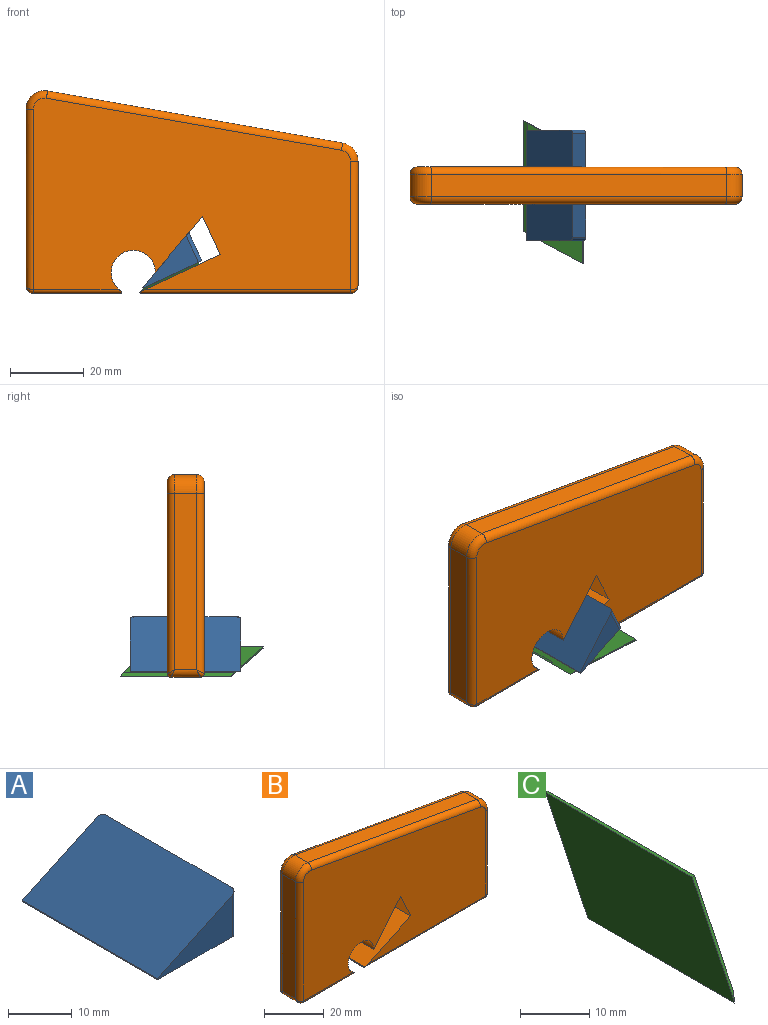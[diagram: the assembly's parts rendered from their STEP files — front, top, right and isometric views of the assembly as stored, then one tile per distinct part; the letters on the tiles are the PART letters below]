
ASSEMBLY  parts=3 mates=2
PART A: 8 faces, bbox 17.5x30x8.4 mm
  f0: plane 30x17.55mm, normal (-0.42,0,0.91), area 580.4mm2, adj f2,f3,f4,f5,f6,f7
  f1: plane 30x17.5mm, normal (0,0,-1), area 524.6mm2, adj f2,f3,f4,f5,f6,f7
  f2: plane 28x8.39mm, normal (1,0,0), area 235mm2, adj f0,f1,f6,f7
  f3: plane 16.55x7.93mm, normal (0,-1,0), area 67.3mm2, adj f0,f1,f5,f7
  f4: plane 16.55x7.93mm, normal (0,1,0), area 67.3mm2, adj f0,f1,f5,f6
  f5: plane 30x0.21mm, normal (-0.98,0,-0.22), area 6.5mm2, adj f0,f1,f3,f4
  f6: cylinder r=1mm len=8.39mm, axis (0,0,1), area 12.9mm2, adj f0,f1,f2,f4
  f7: cylinder r=1mm len=8.39mm, axis (0,0,-1), area 12.9mm2, adj f0,f1,f2,f3
PART B: 35 faces, bbox 90.9x10x55.4 mm
  f0: plane 57x8mm, normal (0,0,-1), area 456mm2, adj f7,f24,f31,f33
  f1: plane 86x51.91mm, normal (0,-1,0), area 3618.9mm2, adj f8,f9,f10,f11,f19,f21,f23,f25
  f2: plane 86x51.91mm, normal (0,1,0), area 3618.9mm2, adj f8,f9,f10,f11,f15,f16,f18,f20
  f3: plane 47.91x6mm, normal (-1,0,0), area 287.5mm2, adj f14,f15,f17,f19
  f4: plane 24x8mm, normal (0,0,-1), area 192mm2, adj f12,f17,f27,f29
  f5: plane 33.8x6mm, normal (1,0,0), area 202.8mm2, adj f13,f22,f24,f26
  f6: plane 80x14.11mm, normal (0.17,0,0.98), area 487.4mm2, adj f13,f14,f18,f23
  f7: plane 9.69x0.47mm, normal (-1,0,0), area 4.3mm2, adj f0,f8,f31,f33
  f8: plane 21.71x10.15mm, normal (-0.42,0,0.91), area 238.8mm2, adj f1,f2,f7,f9,f31,f33
  f9: plane 10.33x10mm, normal (-0.91,0,-0.42), area 113.9mm2, adj f1,f2,f8,f11
  f10: cylinder r=6mm len=12mm, axis (0,-1,0), area 249.8mm2, adj f1,f2,f11,f12,f27,f29
  f11: plane 15.21x12.77mm, normal (0.77,0,-0.64), area 198.6mm2, adj f1,f2,f9,f10
  f12: plane 9.71x0.48mm, normal (1,0,0), area 4.4mm2, adj f4,f10,f27,f29
  f13: cylinder r=5mm len=6mm, axis (0,1,0), area 41.9mm2, adj f5,f6,f20,f25
  f14: cylinder r=5mm len=6mm, axis (0,1,0), area 52.4mm2, adj f3,f6,f16,f21
  f15: cylinder r=2mm len=48.91mm, axis (0,0,-1), area 152.5mm2, adj f2,f3,f16,f28
  f16: torus R=3mm, axis (0,-1,0), area 23.4mm2, adj f2,f14,f15,f18
  f17: cylinder r=2mm len=8mm, axis (0,1,0), area 22.8mm2, adj f3,f4,f28,f30
  f18: cylinder r=2mm len=80.35mm, axis (-0.98,0,0.17), area 255.2mm2, adj f2,f6,f16,f20
  f19: cylinder r=2mm len=48.91mm, axis (0,0,1), area 152.5mm2, adj f1,f3,f21,f30
  f20: torus R=3mm, axis (0,-1,0), area 18.7mm2, adj f2,f13,f18,f22
  f21: torus R=3mm, axis (0,-1,0), area 23.4mm2, adj f1,f14,f19,f23
  f22: cylinder r=2mm len=34.8mm, axis (0,0,1), area 108.2mm2, adj f2,f5,f20,f34
  f23: cylinder r=2mm len=80.35mm, axis (0.98,0,-0.17), area 255.2mm2, adj f1,f6,f21,f25
  f24: cylinder r=2mm len=8mm, axis (0,1,0), area 22.8mm2, adj f0,f5,f32,f34
  f25: torus R=3mm, axis (0,-1,0), area 18.7mm2, adj f1,f13,f23,f26
  f26: cylinder r=2mm len=34.8mm, axis (0,0,-1), area 108.2mm2, adj f1,f5,f25,f32
  f27: cylinder r=1mm len=24mm, axis (1,0,0), area 37.5mm2, adj f2,f4,f10,f12,f28
  f28: bspline ~2.39x2mm, area 3.3mm2, adj f15,f17,f27
  f29: cylinder r=1mm len=24mm, axis (-1,0,0), area 37.5mm2, adj f1,f4,f10,f12,f30
  f30: bspline ~2.1x2mm, area 3.3mm2, adj f17,f19,f29
  f31: cylinder r=1mm len=57mm, axis (-1,0,0), area 89.2mm2, adj f0,f1,f7,f8,f32
  f32: bspline ~2.39x2mm, area 3.3mm2, adj f24,f26,f31
  f33: cylinder r=1mm len=57mm, axis (1,0,0), area 89.2mm2, adj f0,f2,f7,f8,f34
  f34: bspline ~2.39x2mm, area 3.3mm2, adj f22,f24,f33
PART C: 6 faces, bbox 0.5x38.7x18 mm
  f0: plane 30x0.5mm, normal (0,0,1), area 15mm2, adj f1,f2,f3,f4
  f1: plane 18x8.72mm, normal (0,-0.9,0.44), area 9.6mm2, adj f0,f3,f4,f5
  f2: plane 18x8.72mm, normal (0,0.9,-0.44), area 9.6mm2, adj f0,f3,f4,f5
  f3: plane 37.99x16.5mm, normal (1,0,0), area 495mm2, adj f0,f1,f2,f5
  f4: plane 38.72x18mm, normal (-1,0,0), area 540mm2, adj f0,f1,f2,f5
  f5: plane 30.73x1.5mm, normal (0.95,0,-0.32), area 47.4mm2, adj f1,f2,f3,f4
PLACE A rot(axis=(0,-1,0),25deg) t=(-25.37,17.43,-1.69)mm
PLACE B t=(-19.87,7.36,-6.72)mm fixed
PLACE C rot(axis=(-0.54,0,-0.84),180deg) t=(-17.91,-3.71,1.19)mm
MATE planar C.f4 <-> B.f8  axis (0.42,0,-0.91) through (-26.07,0.65,-2.61)mm
MATE planar A.f0 <-> B.f11  axis (-0.77,0,0.64) through (-26.99,2.43,2.3)mm
